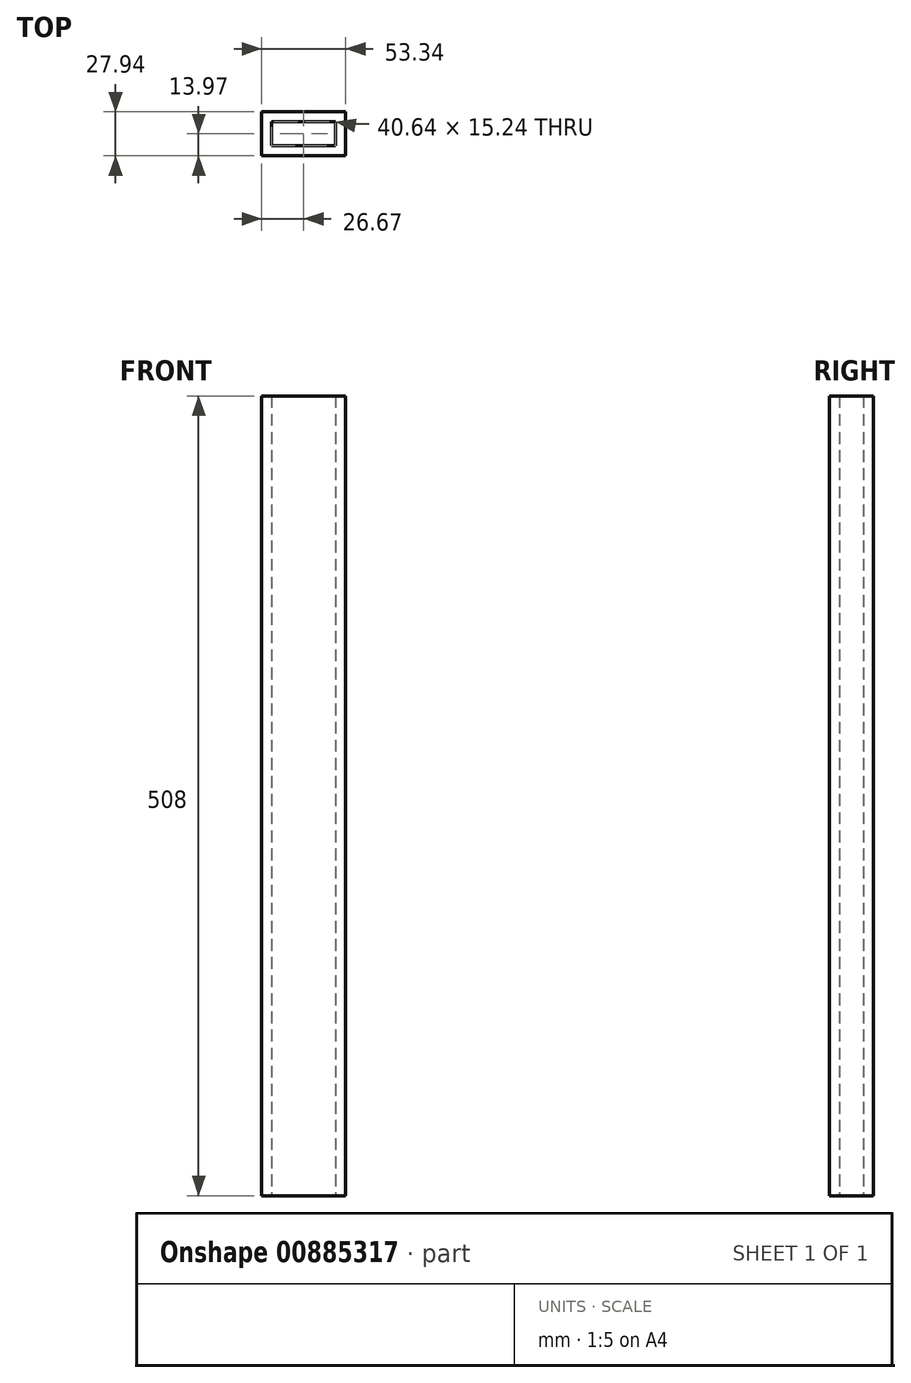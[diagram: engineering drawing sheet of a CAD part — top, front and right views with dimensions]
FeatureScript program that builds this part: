
annotation { "Feature Type Name" : "Feature", "Feature Type Description" : "" }
export const myFeature = defineFeature(function(context is Context, id is Id, definition is map)
    precondition{}
    {
        {
            var Q0;
            Q0=qCreatedBy(makeId("Top.planeOp"),FACE);
            var sketch = newSketch(context, id + "F0", { "sketchPlane" : qUnion([Q0])});
            skLineSegment(sketch, "E0.bottom", {"start": v(-20.32, -7.62) * mm, "end": v(20.32, -7.62) * mm});
            skLineSegment(sketch, "E0.top", {"start": v(-20.32, 7.62) * mm, "end": v(20.32, 7.62) * mm});
            skLineSegment(sketch, "E0.left", {"start": v(-20.32, -7.62) * mm, "end": v(-20.32, 7.62) * mm});
            skLineSegment(sketch, "E0.right", {"start": v(20.32, -7.62) * mm, "end": v(20.32, 7.62) * mm});
            skPoint(sketch, "E0.middle", {"position": v(0, 0) * mm});
            skLineSegment(sketch, "E1.0", {"start": v(-26.67, -13.97) * mm, "end": v(26.67, -13.97) * mm});
            skLineSegment(sketch, "E1.1", {"start": v(-26.67, -13.97) * mm, "end": v(-26.67, 13.97) * mm});
            skLineSegment(sketch, "E1.2", {"start": v(-26.67, 13.97) * mm, "end": v(26.67, 13.97) * mm});
            skLineSegment(sketch, "E1.3", {"start": v(26.67, -13.97) * mm, "end": v(26.67, 13.97) * mm});
            skSolve(sketch);
        }
        {
            var Q0;
            Q0=makeQuery(id+"F0.imprint","IMPRINT",FACE,{"disambiguationData":[TD([[makeQuery(id+"F0.imprint","IMPRINT",EDGE,{"derivedFrom":sQuery(id+"F0.wireOp",EDGE,"E0.bottom")}),-1.0]])]});
            extrude(context, id + "F1", {"entities" : qUnion([Q0]), "depth" : 508 * mm, "offsetDistance" : 25.4 * mm});
        }
    });
